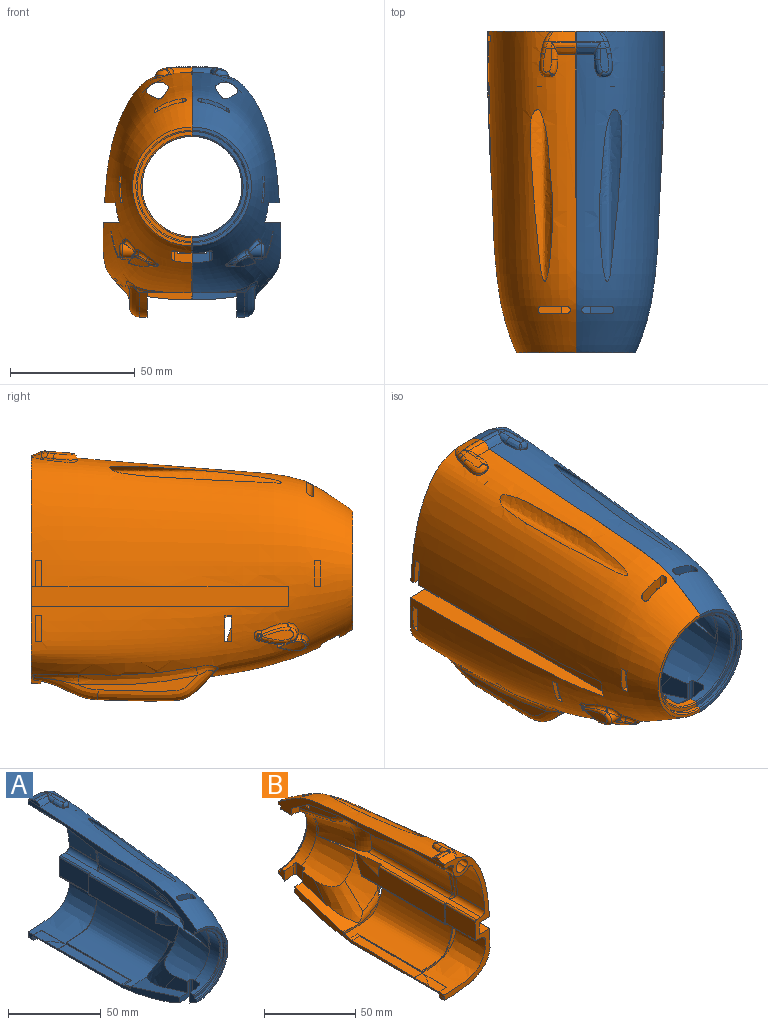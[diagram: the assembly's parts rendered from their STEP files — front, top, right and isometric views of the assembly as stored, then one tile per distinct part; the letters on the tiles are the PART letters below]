
ASSEMBLY  parts=2 mates=1
PART A: 197 faces, bbox 48.4x133.3x102.9 mm
  f0: plane 91.37x35.9mm, normal (0,1,0), area 574.4mm2, adj f1,f15,f20,f22,f23,f49,f51,f52
  f1: extruded ~100.23x9.11mm, area 1167.1mm2, adj f0,f23,f193,f194,f195,f196
  f2: cone r=59.01mm half-angle=77.8deg, axis (0,1,0), area 0mm2, adj f84,f96,f190
  f3: extruded ~0.99x0.39mm, area 0.2mm2, adj f4,f97,f180
  f4: cone r=23.31mm half-angle=48.5deg, axis (0,1,0), area 272mm2, adj f3,f5,f9,f15,f16,f89,f94,f97
  f5: torus R=41.29mm, axis (0,-1,0), area 70.1mm2, adj f4,f99,f111,f126,f133,f182,f184
  f6: plane 62.84x22.1mm, normal (-1,0,0), area 262.5mm2, adj f9,f11,f20,f23,f98,f115,f116,f117
  f7: cone r=23.31mm half-angle=48.5deg, axis (0,1,0), area 2.2mm2, adj f18,f111,f126
  f8: plane 115.6x17.45mm, normal (-1,0,0), area 284.5mm2, adj f21,f23,f27,f29,f36,f45,f47,f54
  f9: cone r=18.78mm half-angle=7deg, axis (0,1,0), area 661.7mm2, adj f4,f6,f13,f14,f15,f54,f114,f115
  f10: plane 6.81x5.3mm, normal (-1,0,0), area 23.5mm2, adj f11,f23,f53,f115,f116,f117,f118,f119
  f11: plane 47.57x23.78mm, normal (0,-1,0), area 93.3mm2, adj f6,f10,f23,f118
  f12: cylinder r=1.2mm len=7.93mm, axis (0,0,-1), area 14.2mm2, adj f13,f23,f53,f115
  f13: plane 10.79x5.27mm, normal (-1,0,0), area 48.3mm2, adj f9,f12,f14,f23,f115
  f14: cylinder r=1.2mm len=11.33mm, axis (0,0,-1), area 19.9mm2, adj f9,f13,f23,f54
  f15: plane 117.87x8.76mm, normal (0,0,1), area 403mm2, adj f0,f4,f9,f16,f17,f80,f92,f93
  f16: plane 70.54x14.79mm, normal (-1,0,0), area 754.8mm2, adj f4,f15,f17,f93,f94,f112,f113
  f17: cylinder r=1mm len=50.8mm, axis (0,-1,0), area 79.8mm2, adj f15,f16,f93,f112
  f18: plane 5.37x1.67mm, normal (1,0,0), area 3.8mm2, adj f7,f99,f111,f126
  f19: plane 2.04x1.51mm, normal (0,1,0), area 0.5mm2, adj f101,f103,f105
  f20: bspline ~67.75x17.92mm, area 191.8mm2, adj f0,f6,f23,f86,f98,f100,f153
  f21: plane 32.03x23.97mm, normal (0,1,0), area 55.6mm2, adj f8,f87,f88,f109,f110,f127,f128
  f22: bspline ~11.69x7.33mm, area 5.3mm2, adj f0,f23,f29,f36,f47,f87
  f23: bspline ~130.13x91.62mm, area 12101.7mm2, adj f0,f1,f6,f8,f10,f11,f12,f13
  f24: bspline ~6.07x5.55mm, area 14.2mm2, adj f23,f56,f67,f68,f178
  f25: bspline ~9.25x5.23mm, area 10.7mm2, adj f23,f57,f64,f173
  f26: cylinder r=0.97mm len=0.94mm, axis (-1,0,0), area 0.3mm2, adj f59,f65,f73
  f27: extruded ~2.55x0.04mm, area 0.1mm2, adj f8,f23,f45
  f28: extruded ~48.06x19.28mm, area 172.9mm2, adj f23,f30,f37,f40,f45,f46,f48
  f29: extruded ~3.5x0.4mm, area 0.1mm2, adj f8,f22,f36,f47
  f30: extruded ~25.83x7.95mm, area 84.5mm2, adj f23,f28,f41,f46,f47,f171
  f31: plane 9.94x8.83mm, normal (0,1,0), area 65.6mm2, adj f23,f32,f34,f35,f120,f122
  f32: cylinder r=1.5mm len=6.69mm, axis (0,0,1), area 28mm2, adj f23,f31,f33,f35
  f33: plane 10.28x9.89mm, normal (0,-1,0), area 75.5mm2, adj f23,f32,f34,f35,f120,f122
  f34: cylinder r=1.5mm len=7mm, axis (0,0,1), area 24.9mm2, adj f23,f31,f33,f122
  f35: plane 9.18x3mm, normal (0,0,1), area 26.6mm2, adj f31,f32,f33,f120
  f36: plane 2.35x0mm, normal (0,1,0), area 0mm2, adj f8,f22,f29,f87
  f37: plane 7.55x2.31mm, normal (0,-0.84,-0.55), area 4mm2, adj f28,f40,f42,f48
  f38: plane 3.37x1.11mm, normal (0,1,0), area 0.9mm2, adj f23,f170,f171
  f39: plane 48.02x6.36mm, normal (1,0,0), area 124.5mm2, adj f40,f41,f43
  f40: bspline ~52.01x14.65mm, area 304.4mm2, adj f28,f37,f39,f41,f42
  f41: bspline ~26.78x11.98mm, area 144.2mm2, adj f30,f39,f40,f44,f170
  f42: bspline ~10.67x4.51mm, area 22.5mm2, adj f23,f37,f40,f43,f48
  f43: bspline ~60.41x7.55mm, area 207.9mm2, adj f23,f39,f42,f44
  f44: bspline ~21.99x5.03mm, area 55mm2, adj f23,f41,f43,f169
  f45: plane 68.06x18.02mm, normal (0,0,-1), area 1224.4mm2, adj f8,f23,f27,f28,f46,f47
  f46: plane 68.17x10.34mm, normal (-1,0,0), area 519.7mm2, adj f28,f30,f45,f47
  f47: plane 18.01x2.8mm, normal (0,-1,0), area 44.3mm2, adj f8,f22,f23,f29,f30,f45,f46
  f48: bspline ~12.46x4.07mm, area 10mm2, adj f23,f28,f37,f42
  f49: plane 103.25x8.04mm, normal (1,0,0), area 830.1mm2, adj f0,f50,f51,f52,f144,f145,f147
  f50: plane 8.08x3.73mm, normal (0,1,0), area 24.2mm2, adj f23,f49,f51,f52
  f51: plane 103.25x8.43mm, normal (0,0,1), area 703.9mm2, adj f0,f23,f49,f50
  f52: plane 103.26x10.53mm, normal (0,0,-1), area 705.8mm2, adj f0,f23,f49,f50,f140,f141,f142,f144
  f53: plane 8.09x7.03mm, normal (0,1,0), area 48.3mm2, adj f10,f12,f23,f115
  f54: plane 11.45x7.02mm, normal (0,-1,0), area 31.8mm2, adj f8,f9,f14,f23,f125,f126
  f55: extruded ~0.57x0.14mm, area 0mm2, adj f63,f68,f69
  f56: cylinder r=2.87mm len=5.65mm, axis (-1,0,0), area 23.3mm2, adj f24,f60,f62,f69,f176,f177
  f57: extruded ~12.26x3.29mm, area 25.9mm2, adj f25,f59,f60,f173,f174
  f58: plane 14.34x4.12mm, normal (1,0,0), area 34.5mm2, adj f59,f61,f62,f63,f71,f72,f73,f74
  f59: bspline ~13.88x3.01mm, area 24mm2, adj f26,f57,f58,f61,f64,f65,f73
  f60: cylinder r=1.25mm len=3.15mm, axis (-1,0,0), area 0.1mm2, adj f56,f57,f61,f175
  f61: torus R=2.5mm, axis (1,0,0), area 0.1mm2, adj f58,f59,f60,f62
  f62: torus R=1.62mm, axis (1,0,0), area 13.4mm2, adj f56,f58,f61,f70
  f63: bspline ~13.91x4.51mm, area 15.9mm2, adj f55,f58,f66,f67,f70,f71,f72
  f64: bspline ~2.11x1.51mm, area 0.6mm2, adj f23,f25,f59,f65
  f65: bspline ~4.24x3.89mm, area 8.2mm2, adj f23,f26,f59,f64,f66,f75
  f66: bspline ~13.72x5.35mm, area 20.2mm2, adj f23,f63,f65,f67,f74
  f67: bspline ~2.1x1.97mm, area 0.5mm2, adj f24,f63,f66,f68
  f68: bspline ~1.34x1.21mm, area 0.5mm2, adj f24,f55,f67,f69
  f69: cylinder r=1.2mm len=0.14mm, axis (-1,0,0), area 0mm2, adj f55,f56,f68,f70
  f70: bspline ~1.53x1.25mm, area 0mm2, adj f62,f63,f69
  f71: bspline ~0.66x0.45mm, area 0mm2, adj f58,f63,f72
  f72: bspline ~0.71x0.71mm, area 0.3mm2, adj f58,f63,f71,f74
  f73: torus R=0.37mm, axis (1,0,0), area 1.3mm2, adj f26,f58,f59,f75
  f74: bspline ~0.47x0.37mm, area 0mm2, adj f58,f66,f72,f75
  f75: bspline ~2.41x1.99mm, area 1.9mm2, adj f58,f65,f73,f74
  f76: bspline ~14.66x11.19mm, area 44.2mm2, adj f77,f134,f135,f136
  f77: cylinder r=0.72mm len=3.32mm, axis (-1,0,0), area 4mm2, adj f23,f76,f79,f134,f136,f173,f174
  f78: cylinder r=2.14mm len=4.15mm, axis (-1,0,0), area 3.4mm2, adj f79,f135,f139
  f79: extruded ~10.16x9.52mm, area 25.4mm2, adj f23,f77,f78,f134,f135,f139
  f80: cylinder r=3mm len=25mm, axis (0,1,0), area 107.7mm2, adj f0,f15,f81,f101,f107,f108
  f81: plane 21.32x0.26mm, normal (-1,0,0), area 3.9mm2, adj f0,f80,f82,f101
  f82: extruded ~34.68x21mm, area 761.7mm2, adj f0,f81,f83,f101
  f83: cylinder r=2mm len=21mm, axis (0,1,0), area 79.3mm2, adj f0,f82,f84,f102
  f84: cylinder r=6.5mm len=83.9mm, axis (0,1,0), area 1260mm2, adj f0,f2,f83,f85,f96,f98,f100,f103
  f85: cylinder r=2mm len=37.3mm, axis (0,1,0), area 111mm2, adj f0,f84,f86,f100
  f86: extruded ~23.79x5.06mm, area 120.9mm2, adj f0,f20,f85,f100
  f87: extruded ~31.96x23mm, area 957.8mm2, adj f0,f8,f21,f22,f36,f88,f129,f130
  f88: cylinder r=3mm len=23.3mm, axis (0,1,0), area 105.6mm2, adj f0,f21,f87,f89,f110
  f89: plane 86.31x4.84mm, normal (0,0,-1), area 376.5mm2, adj f0,f4,f88,f90,f93,f94,f97
  f90: cylinder r=1mm len=23mm, axis (0,1,0), area 36.1mm2, adj f0,f89,f91,f93
  f91: plane 23x12.04mm, normal (-1,0,0), area 276.9mm2, adj f0,f90,f92,f93
  f92: cylinder r=1mm len=23mm, axis (0,1,0), area 36.1mm2, adj f0,f15,f91,f93
  f93: plane 14.04x1.74mm, normal (0,1,0), area 10.5mm2, adj f15,f16,f17,f89,f90,f91,f92,f94
  f94: cylinder r=1mm len=64.37mm, axis (0,-1,0), area 100.1mm2, adj f4,f16,f89,f93
  f95: cylinder r=3mm len=63.67mm, axis (0,-1,0), area 220.6mm2, adj f15,f96,f107,f108,f190
  f96: extruded ~62.44x33.52mm, area 2228.9mm2, adj f2,f84,f95,f104,f105,f106,f190
  f97: cylinder r=3mm len=59.4mm, axis (0,-1,0), area 181.4mm2, adj f3,f4,f89,f99,f110,f179,f180,f181
  f98: extruded ~29.63x6.75mm, area 200mm2, adj f6,f20,f84,f100,f132
  f99: extruded ~54.88x30.03mm, area 2011.9mm2, adj f5,f18,f97,f109,f111,f126,f127,f179
  f100: bspline ~29.86x7.52mm, area 194.3mm2, adj f20,f84,f85,f86,f98
  f101: bspline ~39.66x12.73mm, area 85.7mm2, adj f19,f80,f81,f82,f102,f106,f107
  f102: sphere r=2mm, area 8mm2, adj f83,f101,f103
  f103: torus R=8.5mm, axis (0,-1,0), area 1mm2, adj f19,f84,f102,f104
  f104: bspline ~4.61x4.42mm, area 8.3mm2, adj f84,f96,f103,f105
  f105: bspline ~5.51x5.06mm, area 6.8mm2, adj f19,f96,f104,f106
  f106: bspline ~35.37x12.1mm, area 74.4mm2, adj f96,f101,f105,f107
  f107: bspline ~5.76x2.5mm, area 6.3mm2, adj f80,f95,f101,f106,f108
  f108: torus R=5mm, axis (0,-1,0), area 0.1mm2, adj f80,f95,f107
  f109: bspline ~25.27x22.28mm, area 17.2mm2, adj f21,f99,f110,f127
  f110: torus R=3.3mm, axis (0,-1,0), area 1.5mm2, adj f21,f88,f97,f109
  f111: plane 27.23x9.14mm, normal (0,1,0), area 46.7mm2, adj f5,f7,f18,f99,f126
  f112: plane 7.12x2.05mm, normal (0,-1,0), area 8.4mm2, adj f15,f16,f17,f113
  f113: cone r=18.78mm half-angle=7deg, axis (0,1,0), area 60.3mm2, adj f15,f16,f112
  f114: cone r=20.14mm half-angle=12.6deg, axis (0,1,0), area 740.1mm2, adj f9,f15,f190,f192
  f115: cylinder r=20mm len=40mm, axis (0,-1,0), area 427.1mm2, adj f6,f9,f10,f12,f13,f53,f119
  f116: cylinder r=22mm len=44mm, axis (0,-1,0), area 103.7mm2, adj f6,f10,f117,f118
  f117: plane 44x22mm, normal (0,-1,0), area 100.1mm2, adj f6,f10,f116,f119
  f118: torus R=22.5mm, axis (0,-1,0), area 54.7mm2, adj f6,f10,f11,f116
  f119: torus R=20.5mm, axis (0,-1,0), area 49.8mm2, adj f6,f10,f115,f117
  f120: plane 32.33x15.54mm, normal (-1,0,0), area 210mm2, adj f31,f33,f35,f122,f123,f124,f191,f192
  f121: plane 6.78x0.74mm, normal (0,0,-1), area 3.3mm2, adj f6,f84,f124,f132
  f122: plane 13.95x9.71mm, normal (0,0.57,-0.82), area 85.8mm2, adj f6,f31,f33,f34,f120,f123,f124
  f123: plane 7.63x6.08mm, normal (0,1,0), area 29.9mm2, adj f6,f9,f120,f122,f192
  f124: plane 21.24x6.9mm, normal (0,0.17,-0.99), area 129.1mm2, adj f6,f84,f120,f121,f122,f191
  f125: plane 17.31x12.75mm, normal (-1,0,0), area 111.5mm2, adj f9,f54,f126,f133
  f126: plane 45.17x15.49mm, normal (0,0.3,0.95), area 287.6mm2, adj f5,f7,f8,f18,f54,f99,f111,f125
  f127: plane 50.23x1.24mm, normal (-1,0,0), area 42.8mm2, adj f21,f99,f109,f126,f128
  f128: plane 48.55x6mm, normal (0,0.01,1), area 291.3mm2, adj f8,f21,f126,f127
  f129: plane 17.6x6mm, normal (0,0.01,1), area 74mm2, adj f8,f87,f130,f131
  f130: plane 6.01x0.27mm, normal (0,-1,0), area 1.1mm2, adj f8,f87,f129,f131
  f131: plane 17.6x0.26mm, normal (-1,0,0), area 2.3mm2, adj f87,f129,f130
  f132: bspline ~6.88x0.92mm, area 6.4mm2, adj f6,f84,f98,f121
  f133: bspline ~35.9x32.75mm, area 376.7mm2, adj f4,f5,f9,f125,f126
  f134: bspline ~10.13x8.54mm, area 6.5mm2, adj f76,f77,f79,f135
  f135: bspline ~6.36x4.3mm, area 5.2mm2, adj f76,f78,f79,f134,f136,f138
  f136: bspline ~12.34x5.39mm, area 7.1mm2, adj f76,f77,f135,f137,f174,f175,f176
  f137: bspline ~4.8x3.13mm, area 5.6mm2, adj f23,f136,f138,f177,f178
  f138: bspline ~5x4.44mm, area 12.5mm2, adj f23,f135,f137,f139
  f139: bspline ~5.82x4.68mm, area 8.8mm2, adj f23,f78,f79,f138
  f140: plane 10.44x3.44mm, normal (0,-1,0), area 26.1mm2, adj f23,f52,f142,f143
  f141: plane 10.45x3.46mm, normal (0,1,0), area 26.1mm2, adj f23,f52,f142,f143
  f142: bspline ~12.83x8.38mm, area 26.2mm2, adj f52,f140,f141,f143
  f143: plane 2.54x2.5mm, normal (0,0,-1), area 6.3mm2, adj f23,f140,f141,f142
  f144: plane 2.5x0.07mm, normal (0,1,0), area 0.2mm2, adj f49,f52,f146,f147
  f145: plane 2.5x0.07mm, normal (0,-1,0), area 0.2mm2, adj f49,f52,f146,f147
  f146: plane 2.5x0.07mm, normal (1,0,0), area 0.2mm2, adj f52,f144,f145,f147
  f147: plane 2.5x2.5mm, normal (0,0,1), area 6.3mm2, adj f49,f144,f145,f146
  f148: bspline ~18.19x5.24mm, area 27.2mm2, adj f149,f150,f151,f152
  f149: plane 10.59x3.25mm, normal (0,1,0), area 26.2mm2, adj f23,f148,f150,f151
  f150: plane 3.16x2.51mm, normal (0,0,-1), area 6.2mm2, adj f23,f148,f149,f152
  f151: plane 3.18x2.51mm, normal (0,0,1), area 6.2mm2, adj f23,f148,f149,f152
  f152: plane 10.59x3.21mm, normal (0,-1,0), area 26.2mm2, adj f23,f148,f150,f151
  f153: plane 10.35x3.23mm, normal (-1,0,0), area 13.2mm2, adj f0,f20,f158,f159,f160,f172
  f154: bspline ~14.66x7.37mm, area 27.2mm2, adj f159,f163,f164,f166,f167
  f155: plane 1.93x0.16mm, normal (-1,0,0), area 0.1mm2, adj f23,f156,f160,f167
  f156: extruded ~9.55x7.3mm, area 11.9mm2, adj f23,f155,f157,f163,f164,f165,f166,f167
  f157: extruded ~5.56x1.59mm, area 4.1mm2, adj f23,f156,f161,f162,f163
  f158: bspline ~11.41x4.32mm, area 47.8mm2, adj f0,f153,f159,f161
  f159: bspline ~14.65x2.51mm, area 6.7mm2, adj f153,f154,f158,f162,f168,f172
  f160: bspline ~10.37x5.28mm, area 28.7mm2, adj f23,f153,f155,f167,f168,f172
  f161: bspline ~7.45x4.79mm, area 8.8mm2, adj f0,f23,f157,f158,f162
  f162: bspline ~4.46x2.46mm, area 6.1mm2, adj f157,f159,f161,f163
  f163: bspline ~5.85x2.73mm, area 7.3mm2, adj f154,f156,f157,f162,f164
  f164: bspline ~10.21x5.42mm, area 32.6mm2, adj f154,f156,f163,f165
  f165: bspline ~2.1x2.05mm, area 1.1mm2, adj f156,f164,f166
  f166: bspline ~7.41x3.61mm, area 22mm2, adj f154,f156,f165,f167
  f167: bspline ~14.08x3.21mm, area 14.1mm2, adj f154,f155,f156,f160,f166,f168
  f168: bspline ~4.42x3.14mm, area 1.7mm2, adj f159,f160,f167,f172
  f169: bspline ~2.07x1.67mm, area 0.7mm2, adj f23,f44,f170
  f170: bspline ~2.91x1.63mm, area 2.3mm2, adj f38,f41,f169,f171
  f171: plane 3.11x0.58mm, normal (0,0.72,-0.69), area 1.4mm2, adj f23,f30,f38,f170
  f172: bspline ~12.52x2.18mm, area 20.1mm2, adj f153,f159,f160,f168
  f173: cylinder r=0.4mm len=1.89mm, axis (-1,0,0), area 1.2mm2, adj f23,f25,f57,f77,f174
  f174: bspline ~7.12x1.7mm, area 3.5mm2, adj f57,f77,f136,f173,f175
  f175: bspline ~0.39x0.31mm, area 0mm2, adj f60,f136,f174,f176
  f176: bspline ~2.41x1.82mm, area 1.4mm2, adj f56,f136,f175,f177
  f177: bspline ~1.68x1.3mm, area 0.7mm2, adj f56,f137,f176,f178
  f178: bspline ~1.74x1.03mm, area 0.3mm2, adj f24,f137,f177
  f179: plane 10.52x4.34mm, normal (0,-1,0), area 20mm2, adj f23,f97,f99,f181,f183,f184
  f180: plane 10.52x5.47mm, normal (0,1,0), area 23.8mm2, adj f3,f4,f23,f97,f181,f182,f183,f184
  f181: bspline ~8.38x6.49mm, area 1.1mm2, adj f97,f179,f180,f183
  f182: bspline ~8.52x8.38mm, area 5.7mm2, adj f4,f5,f180,f184
  f183: plane 2.76x2.5mm, normal (0,0,-1), area 6.2mm2, adj f23,f179,f180,f181
  f184: plane 2.97x2.51mm, normal (0,0,1), area 5.6mm2, adj f5,f23,f99,f179,f180,f182
  f185: bspline ~13.13x7.33mm, area 26.3mm2, adj f186,f187,f188,f189
  f186: plane 10.5x2.8mm, normal (0,1,0), area 26.2mm2, adj f23,f185,f187,f188
  f187: plane 2.51x2.5mm, normal (0,0,-1), area 6.2mm2, adj f23,f185,f186,f189
  f188: plane 2.53x2.5mm, normal (0,0,1), area 6.2mm2, adj f23,f185,f186,f189
  f189: plane 10.51x2.78mm, normal (0,-1,0), area 26.2mm2, adj f23,f185,f187,f188
  f190: torus R=40.03mm, axis (0,-1,0), area 476.2mm2, adj f2,f15,f84,f95,f96,f114,f191
  f191: bspline ~14.89x14.5mm, area 76.9mm2, adj f84,f120,f124,f190,f192
  f192: bspline ~62.12x17.67mm, area 103.4mm2, adj f9,f114,f120,f123,f191
  f193: plane 7.08x2.16mm, normal (0,1,0), area 3.6mm2, adj f1,f194
  f194: cylinder r=4mm len=22mm, axis (0,1,0), area 188.9mm2, adj f0,f1,f193
  f195: cylinder r=4mm len=22mm, axis (0,1,0), area 243.2mm2, adj f0,f1,f196
  f196: plane 7.39x4.9mm, normal (0,1,0), area 6.8mm2, adj f1,f195
PART B: 197 faces, bbox 48.4x136.5x102.9 mm
  f0: plane 91.37x35.9mm, normal (0,-1,0), area 572.1mm2, adj f1,f15,f20,f22,f23,f49,f50,f52
  f1: extruded ~100.23x9.11mm, area 1167.1mm2, adj f0,f23,f193,f194,f195,f196
  f2: cone r=59.01mm half-angle=77.8deg, axis (0,-1,0), area 0mm2, adj f85,f96,f190
  f3: extruded ~0.99x0.39mm, area 0.2mm2, adj f4,f97,f180
  f4: cone r=23.31mm half-angle=48.5deg, axis (0,-1,0), area 272mm2, adj f3,f5,f9,f15,f16,f90,f94,f97
  f5: torus R=41.29mm, axis (0,1,0), area 70.1mm2, adj f4,f99,f111,f126,f133,f182,f183
  f6: plane 61.74x21mm, normal (-1,0,0), area 262.5mm2, adj f9,f11,f20,f23,f98,f115,f116,f117
  f7: cone r=23.31mm half-angle=48.5deg, axis (0,-1,0), area 2.2mm2, adj f18,f111,f126
  f8: plane 115.6x17.45mm, normal (-1,0,0), area 284.5mm2, adj f21,f23,f27,f30,f36,f45,f47,f53
  f9: cone r=18.78mm half-angle=7deg, axis (0,-1,0), area 661.7mm2, adj f4,f6,f12,f13,f15,f53,f114,f115
  f10: plane 6.81x5.3mm, normal (-1,0,0), area 23.5mm2, adj f11,f23,f54,f115,f116,f117,f118,f119
  f11: plane 47.57x23.78mm, normal (0,1,0), area 93.3mm2, adj f6,f10,f23,f118
  f12: plane 10.79x5.27mm, normal (-1,0,0), area 48.3mm2, adj f9,f13,f14,f23,f115
  f13: cylinder r=1.2mm len=11.33mm, axis (0,0,-1), area 19.9mm2, adj f9,f12,f23,f53
  f14: cylinder r=1.2mm len=7.93mm, axis (0,0,-1), area 14.2mm2, adj f12,f23,f54,f115
  f15: plane 117.87x8.76mm, normal (0,0,1), area 403mm2, adj f0,f4,f9,f16,f17,f80,f81,f93
  f16: plane 70.54x14.79mm, normal (-1,0,0), area 754.8mm2, adj f4,f15,f17,f93,f94,f112,f113
  f17: cylinder r=1mm len=50.8mm, axis (0,1,0), area 79.8mm2, adj f15,f16,f93,f112
  f18: plane 5.37x1.67mm, normal (1,0,0), area 3.8mm2, adj f7,f99,f111,f126
  f19: plane 2.04x1.51mm, normal (0,-1,0), area 0.5mm2, adj f101,f103,f105
  f20: bspline ~67.75x17.92mm, area 190.3mm2, adj f0,f6,f23,f87,f98,f100,f153
  f21: plane 32.1x23.97mm, normal (0,-1,0), area 55.6mm2, adj f8,f88,f89,f109,f110,f127,f128
  f22: bspline ~11.69x7.33mm, area 5.3mm2, adj f0,f23,f27,f36,f45,f88
  f23: bspline ~130.13x91.62mm, area 12101.6mm2, adj f0,f1,f6,f8,f10,f11,f12,f13
  f24: bspline ~6.3x5.83mm, area 14.2mm2, adj f23,f57,f67,f68,f178
  f25: bspline ~9.25x5.23mm, area 10.7mm2, adj f23,f55,f64,f173
  f26: cylinder r=0.97mm len=0.94mm, axis (-1,0,0), area 0.3mm2, adj f59,f65,f73
  f27: extruded ~3.5x0.4mm, area 0.1mm2, adj f8,f22,f36,f45
  f28: extruded ~25.83x7.95mm, area 84.5mm2, adj f23,f29,f41,f45,f46,f171
  f29: extruded ~48.06x19.28mm, area 172.9mm2, adj f23,f28,f38,f40,f46,f47,f48
  f30: extruded ~2.55x0.04mm, area 0.1mm2, adj f8,f23,f47
  f31: plane 9.94x8.83mm, normal (0,-1,0), area 65.6mm2, adj f23,f32,f34,f35,f120,f122
  f32: cylinder r=1.5mm len=6.69mm, axis (0,0,1), area 28mm2, adj f23,f31,f33,f35
  f33: plane 10.28x9.89mm, normal (0,1,0), area 75.5mm2, adj f23,f32,f34,f35,f120,f122
  f34: cylinder r=1.5mm len=7mm, axis (0,0,1), area 24.9mm2, adj f23,f31,f33,f122
  f35: plane 9.18x3mm, normal (0,0,1), area 26.6mm2, adj f31,f32,f33,f120
  f36: plane 2.35x0mm, normal (0,-1,0), area 0mm2, adj f8,f22,f27,f88
  f37: plane 3.37x1.11mm, normal (0,-1,0), area 0.9mm2, adj f23,f170,f171
  f38: plane 7.55x2.31mm, normal (0,0.84,-0.55), area 4mm2, adj f29,f40,f42,f48
  f39: plane 48.02x6.36mm, normal (1,0,0), area 124.5mm2, adj f40,f41,f43
  f40: bspline ~52.01x14.65mm, area 304.4mm2, adj f29,f38,f39,f41,f42
  f41: bspline ~26.78x11.98mm, area 144.2mm2, adj f28,f39,f40,f44,f170
  f42: bspline ~10.67x4.51mm, area 22.5mm2, adj f23,f38,f40,f43,f48
  f43: bspline ~60.41x7.55mm, area 207.9mm2, adj f23,f39,f42,f44
  f44: bspline ~21.99x5.03mm, area 55mm2, adj f23,f41,f43,f169
  f45: plane 18.01x2.8mm, normal (0,1,0), area 44.3mm2, adj f8,f22,f23,f27,f28,f46,f47
  f46: plane 68.17x10.34mm, normal (-1,0,0), area 519.7mm2, adj f28,f29,f45,f47
  f47: plane 68.06x18.02mm, normal (0,0,-1), area 1224.4mm2, adj f8,f23,f29,f30,f45,f46
  f48: bspline ~12.46x4.07mm, area 10mm2, adj f23,f29,f38,f42
  f49: plane 103.25x8.04mm, normal (1,0,0), area 830.1mm2, adj f0,f50,f51,f52,f144,f145,f147
  f50: plane 103.25x10.52mm, normal (0,0,-1), area 705.8mm2, adj f0,f23,f49,f51,f140,f141,f142,f144
  f51: plane 8.08x3.73mm, normal (0,-1,0), area 24.2mm2, adj f23,f49,f50,f52
  f52: plane 103.25x8.43mm, normal (0,0,1), area 703.9mm2, adj f0,f23,f49,f51
  f53: plane 11.45x7.02mm, normal (0,1,0), area 31.8mm2, adj f8,f9,f13,f23,f125,f126
  f54: plane 8.09x7.03mm, normal (0,-1,0), area 48.3mm2, adj f10,f14,f23,f115
  f55: extruded ~12.26x3.29mm, area 25.9mm2, adj f25,f59,f60,f173,f174
  f56: extruded ~0.57x0.14mm, area 0mm2, adj f63,f68,f69
  f57: cylinder r=2.87mm len=5.65mm, axis (-1,0,0), area 23.3mm2, adj f24,f60,f62,f69,f176,f177
  f58: plane 14.18x3.96mm, normal (1,0,0), area 34.5mm2, adj f59,f61,f62,f63,f71,f72,f73,f74
  f59: bspline ~13.88x3.01mm, area 24mm2, adj f26,f55,f58,f61,f64,f65,f73
  f60: cylinder r=1.25mm len=3.15mm, axis (-1,0,0), area 0.1mm2, adj f55,f57,f61,f175
  f61: torus R=2.5mm, axis (1,0,0), area 0.1mm2, adj f58,f59,f60,f62
  f62: torus R=1.62mm, axis (1,0,0), area 13.4mm2, adj f57,f58,f61,f70
  f63: bspline ~13.91x4.51mm, area 15.9mm2, adj f56,f58,f66,f67,f70,f71,f72
  f64: bspline ~2.7x1.76mm, area 0.6mm2, adj f23,f25,f59,f65
  f65: bspline ~4.24x3.89mm, area 8.2mm2, adj f23,f26,f59,f64,f66,f75
  f66: bspline ~13.72x5.35mm, area 20.2mm2, adj f23,f63,f65,f67,f74
  f67: bspline ~2.1x1.97mm, area 0.5mm2, adj f24,f63,f66,f68
  f68: bspline ~1.34x1.21mm, area 0.5mm2, adj f24,f56,f67,f69
  f69: cylinder r=1.2mm len=0.14mm, axis (-1,0,0), area 0mm2, adj f56,f57,f68,f70
  f70: bspline ~1.53x1.25mm, area 0mm2, adj f62,f63,f69
  f71: bspline ~0.46x0.27mm, area 0mm2, adj f58,f63,f72
  f72: bspline ~0.71x0.71mm, area 0.3mm2, adj f58,f63,f71,f74
  f73: torus R=0.37mm, axis (1,0,0), area 1.3mm2, adj f26,f58,f59,f75
  f74: bspline ~0.54x0.42mm, area 0mm2, adj f58,f66,f72,f75
  f75: bspline ~2.41x1.99mm, area 1.9mm2, adj f58,f65,f73,f74
  f76: bspline ~14.66x11.19mm, area 44.2mm2, adj f78,f134,f135,f136
  f77: extruded ~10.16x9.52mm, area 25.4mm2, adj f23,f78,f79,f134,f135,f139
  f78: cylinder r=0.72mm len=3.32mm, axis (-1,0,0), area 4mm2, adj f23,f76,f77,f134,f136,f173,f174
  f79: cylinder r=2.14mm len=4.15mm, axis (-1,0,0), area 3.4mm2, adj f77,f135,f139
  f80: cylinder r=1mm len=23mm, axis (0,-1,0), area 36.1mm2, adj f0,f15,f92,f93
  f81: cylinder r=3mm len=25mm, axis (0,-1,0), area 107.7mm2, adj f0,f15,f82,f101,f107,f108
  f82: plane 21.32x0.26mm, normal (-1,0,0), area 3.9mm2, adj f0,f81,f83,f101
  f83: extruded ~34.68x21mm, area 761.7mm2, adj f0,f82,f84,f101
  f84: cylinder r=2mm len=21mm, axis (0,-1,0), area 79.3mm2, adj f0,f83,f85,f102
  f85: cylinder r=6.5mm len=83.9mm, axis (0,-1,0), area 1260mm2, adj f0,f2,f84,f86,f96,f98,f100,f103
  f86: cylinder r=2mm len=37.3mm, axis (0,-1,0), area 111mm2, adj f0,f85,f87,f100
  f87: extruded ~23.79x5.06mm, area 120.9mm2, adj f0,f20,f86,f100
  f88: extruded ~31.96x23mm, area 957.8mm2, adj f0,f8,f21,f22,f36,f89,f129,f130
  f89: cylinder r=3mm len=23.3mm, axis (0,-1,0), area 105.6mm2, adj f0,f21,f88,f90,f110
  f90: plane 86.31x4.84mm, normal (0,0,-1), area 376.5mm2, adj f0,f4,f89,f91,f93,f94,f97
  f91: cylinder r=1mm len=23mm, axis (0,-1,0), area 36.1mm2, adj f0,f90,f92,f93
  f92: plane 23x12.04mm, normal (-1,0,0), area 276.9mm2, adj f0,f80,f91,f93
  f93: plane 14.04x1.74mm, normal (0,-1,0), area 10.5mm2, adj f15,f16,f17,f80,f90,f91,f92,f94
  f94: cylinder r=1mm len=64.37mm, axis (0,1,0), area 100.1mm2, adj f4,f16,f90,f93
  f95: cylinder r=3mm len=63.67mm, axis (0,1,0), area 220.6mm2, adj f15,f96,f107,f108,f190
  f96: extruded ~62.44x33.52mm, area 2228.9mm2, adj f2,f85,f95,f104,f105,f106,f190
  f97: cylinder r=3mm len=59.4mm, axis (0,1,0), area 181.4mm2, adj f3,f4,f90,f99,f110,f179,f180,f181
  f98: extruded ~29.63x6.75mm, area 200mm2, adj f6,f20,f85,f100,f132
  f99: extruded ~54.88x30.03mm, area 2011.9mm2, adj f5,f18,f97,f109,f111,f126,f127,f179
  f100: bspline ~30x8.91mm, area 194.2mm2, adj f20,f85,f86,f87,f98
  f101: bspline ~38.32x12.14mm, area 85.7mm2, adj f19,f81,f82,f83,f102,f106,f107
  f102: sphere r=2mm, area 8mm2, adj f84,f101,f103
  f103: torus R=8.5mm, axis (0,1,0), area 1mm2, adj f19,f85,f102,f104
  f104: bspline ~4.61x4.42mm, area 8.3mm2, adj f85,f96,f103,f105
  f105: bspline ~5.51x5.06mm, area 6.8mm2, adj f19,f96,f104,f106
  f106: bspline ~36.3x12.82mm, area 74.4mm2, adj f96,f101,f105,f107
  f107: bspline ~5.76x2.5mm, area 6.3mm2, adj f81,f95,f101,f106,f108
  f108: torus R=5mm, axis (0,1,0), area 0.1mm2, adj f81,f95,f107
  f109: bspline ~25.27x22.28mm, area 17.2mm2, adj f21,f99,f110,f127
  f110: torus R=3.3mm, axis (0,1,0), area 1.5mm2, adj f21,f89,f97,f109
  f111: plane 27.23x9.14mm, normal (0,-1,0), area 46.7mm2, adj f5,f7,f18,f99,f126
  f112: plane 7.12x2.05mm, normal (0,1,0), area 8.4mm2, adj f15,f16,f17,f113
  f113: cone r=18.78mm half-angle=7deg, axis (0,-1,0), area 60.3mm2, adj f15,f16,f112
  f114: cone r=20.14mm half-angle=12.6deg, axis (0,-1,0), area 740.1mm2, adj f9,f15,f190,f192
  f115: cylinder r=20mm len=40mm, axis (0,1,0), area 427.1mm2, adj f6,f9,f10,f12,f14,f54,f119
  f116: cylinder r=22mm len=44mm, axis (0,1,0), area 103.7mm2, adj f6,f10,f117,f118
  f117: plane 44x22mm, normal (0,1,0), area 100.1mm2, adj f6,f10,f116,f119
  f118: torus R=22.5mm, axis (0,1,0), area 54.7mm2, adj f6,f10,f11,f116
  f119: torus R=20.5mm, axis (0,1,0), area 49.8mm2, adj f6,f10,f115,f117
  f120: plane 32.33x15.54mm, normal (-1,0,0), area 210mm2, adj f31,f33,f35,f122,f123,f124,f191,f192
  f121: plane 6.78x0.74mm, normal (0,0,-1), area 3.3mm2, adj f6,f85,f124,f132
  f122: plane 13.95x9.71mm, normal (0,-0.57,-0.82), area 85.8mm2, adj f6,f31,f33,f34,f120,f123,f124
  f123: plane 7.63x6.08mm, normal (0,-1,0), area 29.9mm2, adj f6,f9,f120,f122,f192
  f124: plane 21.24x6.9mm, normal (0,-0.17,-0.99), area 129.1mm2, adj f6,f85,f120,f121,f122,f191
  f125: plane 17.31x12.75mm, normal (-1,0,0), area 111.5mm2, adj f9,f53,f126,f133
  f126: plane 45.17x15.49mm, normal (0,-0.3,0.95), area 287.6mm2, adj f5,f7,f8,f18,f53,f99,f111,f125
  f127: plane 50.23x1.24mm, normal (-1,0,0), area 42.8mm2, adj f21,f99,f109,f126,f128
  f128: plane 48.55x6mm, normal (0,-0.01,1), area 291.3mm2, adj f8,f21,f126,f127
  f129: plane 17.6x6mm, normal (0,-0.01,1), area 74mm2, adj f8,f88,f130,f131
  f130: plane 6.01x0.27mm, normal (0,1,0), area 1.1mm2, adj f8,f88,f129,f131
  f131: plane 17.6x0.26mm, normal (-1,0,0), area 2.3mm2, adj f88,f129,f130
  f132: bspline ~6.88x0.92mm, area 6.4mm2, adj f6,f85,f98,f121
  f133: bspline ~35.9x32.75mm, area 376.7mm2, adj f4,f5,f9,f125,f126
  f134: bspline ~10.13x8.54mm, area 6.5mm2, adj f76,f77,f78,f135
  f135: bspline ~6.36x4.3mm, area 5.2mm2, adj f76,f77,f79,f134,f136,f138
  f136: bspline ~11.84x5.04mm, area 7.1mm2, adj f76,f78,f135,f137,f174,f175,f176
  f137: bspline ~4.8x3.13mm, area 5.6mm2, adj f23,f136,f138,f177,f178
  f138: bspline ~5x4.44mm, area 12.5mm2, adj f23,f135,f137,f139
  f139: bspline ~5.82x4.68mm, area 8.8mm2, adj f23,f77,f79,f138
  f140: plane 10.44x3.37mm, normal (0,1,0), area 26.1mm2, adj f23,f50,f142,f143
  f141: plane 10.43x3.38mm, normal (0,-1,0), area 26.1mm2, adj f23,f50,f142,f143
  f142: bspline ~12.86x7.33mm, area 26.2mm2, adj f50,f140,f141,f143
  f143: plane 2.51x2.5mm, normal (0,0,-1), area 6.3mm2, adj f23,f140,f141,f142
  f144: plane 2.5x0.07mm, normal (0,-1,0), area 0.2mm2, adj f49,f50,f146,f147
  f145: plane 2.5x0.07mm, normal (0,1,0), area 0.2mm2, adj f49,f50,f146,f147
  f146: plane 2.5x0.07mm, normal (1,0,0), area 0.2mm2, adj f50,f144,f145,f147
  f147: plane 2.5x2.5mm, normal (0,0,1), area 6.3mm2, adj f49,f144,f145,f146
  f148: bspline ~18.19x5.24mm, area 27.2mm2, adj f149,f150,f151,f152
  f149: plane 3.18x2.51mm, normal (0,0,1), area 6.3mm2, adj f23,f148,f150,f151
  f150: plane 10.59x3.25mm, normal (0,-1,0), area 26.2mm2, adj f23,f148,f149,f152
  f151: plane 10.59x3.21mm, normal (0,1,0), area 26.2mm2, adj f23,f148,f149,f152
  f152: plane 3.16x2.51mm, normal (0,0,-1), area 6.2mm2, adj f23,f148,f150,f151
  f153: plane 10.35x3.23mm, normal (-1,0,0), area 13.2mm2, adj f0,f20,f158,f159,f160,f172
  f154: bspline ~14.66x7.37mm, area 27.2mm2, adj f159,f163,f164,f166,f167
  f155: plane 1.93x0.16mm, normal (-1,0,0), area 0.1mm2, adj f23,f156,f160,f167
  f156: extruded ~9.55x7.3mm, area 11.9mm2, adj f23,f155,f157,f163,f164,f165,f166,f167
  f157: extruded ~5.56x1.59mm, area 4.1mm2, adj f23,f156,f161,f162,f163
  f158: bspline ~11.41x4.32mm, area 47.8mm2, adj f0,f153,f159,f161
  f159: bspline ~14.65x2.51mm, area 6.7mm2, adj f153,f154,f158,f162,f168,f172
  f160: bspline ~10.37x5.28mm, area 28.7mm2, adj f23,f153,f155,f167,f168,f172
  f161: bspline ~7.45x4.79mm, area 8.8mm2, adj f0,f23,f157,f158,f162
  f162: bspline ~4.46x2.46mm, area 6.1mm2, adj f157,f159,f161,f163
  f163: bspline ~5.92x2.84mm, area 7.3mm2, adj f154,f156,f157,f162,f164
  f164: bspline ~10.21x5.42mm, area 32.6mm2, adj f154,f156,f163,f165
  f165: bspline ~2.1x2.05mm, area 1.1mm2, adj f156,f164,f166
  f166: bspline ~7.41x3.61mm, area 22mm2, adj f154,f156,f165,f167
  f167: bspline ~14.08x3.21mm, area 14.1mm2, adj f154,f155,f156,f160,f166,f168
  f168: bspline ~4.42x3.14mm, area 1.7mm2, adj f159,f160,f167,f172
  f169: bspline ~1.94x1.61mm, area 0.7mm2, adj f23,f44,f170
  f170: bspline ~2.91x1.63mm, area 2.3mm2, adj f37,f41,f169,f171
  f171: plane 3.11x0.58mm, normal (0,-0.72,-0.69), area 1.4mm2, adj f23,f28,f37,f170
  f172: bspline ~12.52x2.18mm, area 20.1mm2, adj f153,f159,f160,f168
  f173: cylinder r=0.4mm len=1.89mm, axis (-1,0,0), area 1.2mm2, adj f23,f25,f55,f78,f174
  f174: bspline ~6.11x1.43mm, area 3.5mm2, adj f55,f78,f136,f173,f175
  f175: bspline ~0.39x0.31mm, area 0mm2, adj f60,f136,f174,f176
  f176: bspline ~2.91x1.9mm, area 1.4mm2, adj f57,f136,f175,f177
  f177: bspline ~1.68x1.3mm, area 0.7mm2, adj f57,f137,f176,f178
  f178: bspline ~1.74x1.03mm, area 0.3mm2, adj f24,f137,f177
  f179: plane 10.52x4.34mm, normal (0,1,0), area 20mm2, adj f23,f97,f99,f181,f183,f184
  f180: plane 10.52x5.47mm, normal (0,-1,0), area 23.8mm2, adj f3,f4,f23,f97,f181,f182,f183,f184
  f181: bspline ~8.38x6.49mm, area 1.1mm2, adj f97,f179,f180,f184
  f182: bspline ~8.52x8.38mm, area 5.7mm2, adj f4,f5,f180,f183
  f183: plane 2.97x2.51mm, normal (0,0,1), area 5.6mm2, adj f5,f23,f99,f179,f180,f182
  f184: plane 2.76x2.5mm, normal (0,0,-1), area 6.2mm2, adj f23,f179,f180,f181
  f185: bspline ~13.13x7.33mm, area 26.3mm2, adj f186,f187,f188,f189
  f186: plane 2.53x2.5mm, normal (0,0,1), area 6.2mm2, adj f23,f185,f187,f188
  f187: plane 10.5x2.8mm, normal (0,-1,0), area 26.2mm2, adj f23,f185,f186,f189
  f188: plane 10.51x2.78mm, normal (0,1,0), area 26.2mm2, adj f23,f185,f186,f189
  f189: plane 2.51x2.5mm, normal (0,0,-1), area 6.2mm2, adj f23,f185,f187,f188
  f190: torus R=40.03mm, axis (0,1,0), area 476.2mm2, adj f2,f15,f85,f95,f96,f114,f191
  f191: bspline ~14.39x13.67mm, area 76.9mm2, adj f85,f120,f124,f190,f192
  f192: bspline ~69.77x19.52mm, area 103.4mm2, adj f9,f114,f120,f123,f191
  f193: plane 7.08x2.16mm, normal (0,-1,0), area 3.6mm2, adj f1,f194
  f194: cylinder r=4mm len=22mm, axis (0,-1,0), area 188.9mm2, adj f0,f1,f193
  f195: cylinder r=4mm len=22mm, axis (0,-1,0), area 243.2mm2, adj f0,f1,f196
  f196: plane 7.39x4.9mm, normal (0,-1,0), area 6.8mm2, adj f1,f195
PLACE A rot(axis=(0,0,-1),0deg) t=(-32.54,-82.11,37.2)mm
PLACE B rot(axis=(0,0,1),180deg) t=(-32.54,-82.11,37.2)mm
MATE parallel B.f10 <-> A.f10  axis (1,0,0) through (-32.54,-78.83,14.21)mm
